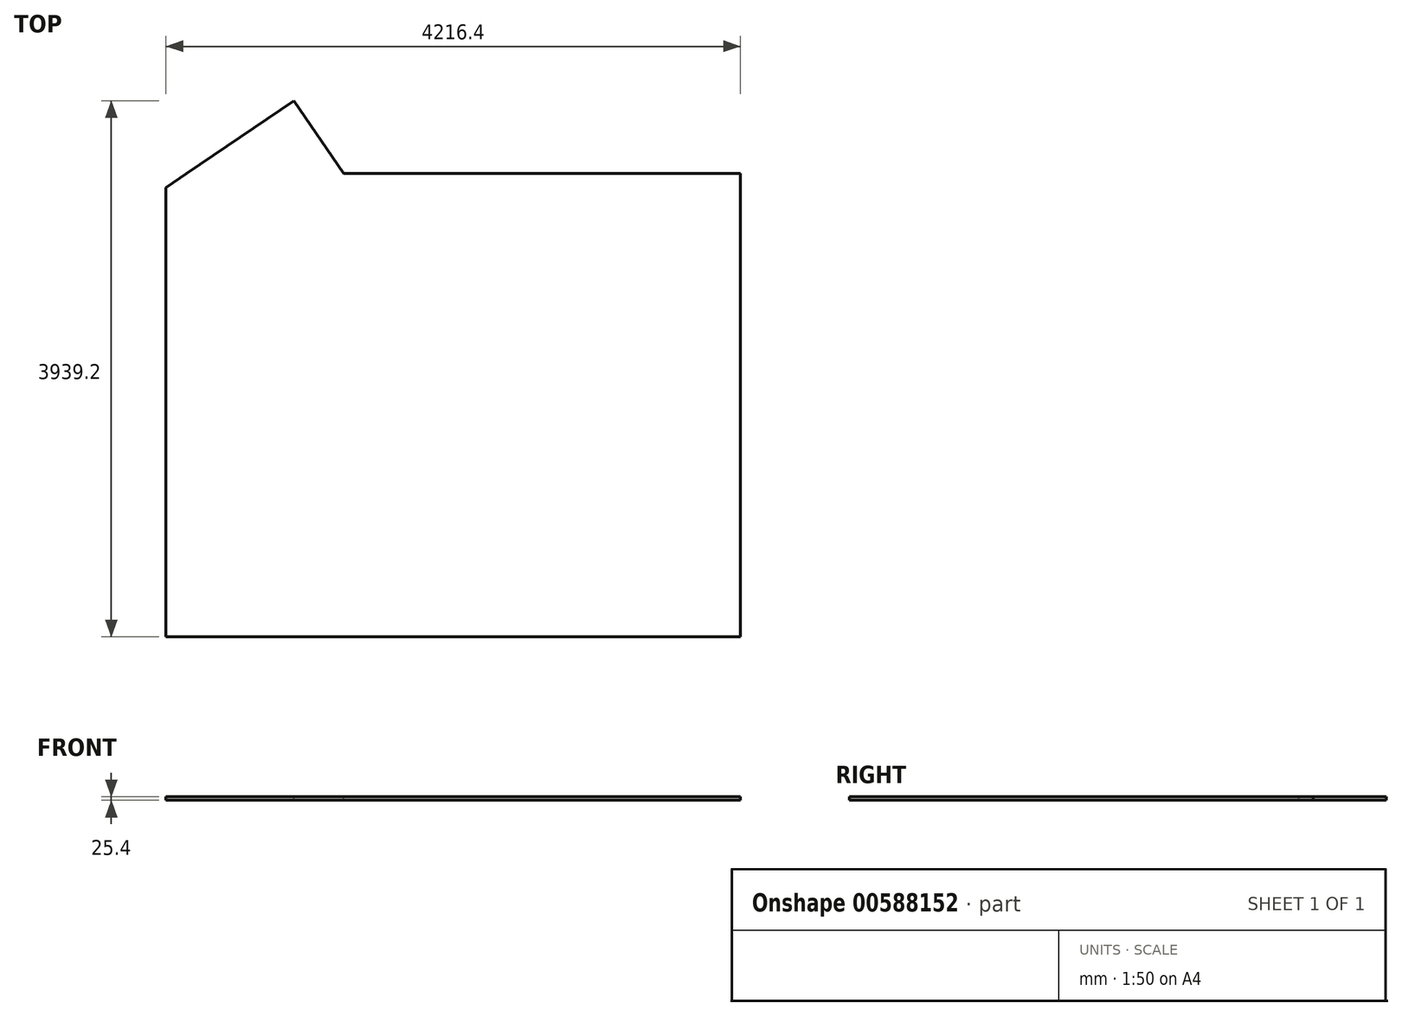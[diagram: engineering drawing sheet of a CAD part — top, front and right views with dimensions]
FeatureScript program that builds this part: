
annotation { "Feature Type Name" : "Feature", "Feature Type Description" : "" }
export const myFeature = defineFeature(function(context is Context, id is Id, definition is map)
    precondition{}
    {
        {
            var Q0;
            Q0=qCreatedBy(makeId("Top.planeOp"),FACE);
            var sketch = newSketch(context, id + "F0", { "sketchPlane" : qUnion([Q0])});
            skLineSegment(sketch, "E0.bottom", {"start": v(2108.2, 1701.8) * mm, "end": v(-2108.2, 1701.8) * mm});
            skLineSegment(sketch, "E0.top", {"start": v(2108.2, -1701.8) * mm, "end": v(-2108.2, -1701.8) * mm});
            skLineSegment(sketch, "E0.left", {"start": v(2108.2, 1701.8) * mm, "end": v(2108.2, -1701.8) * mm});
            skLineSegment(sketch, "E0.right", {"start": v(-2108.2, 1701.8) * mm, "end": v(-2108.2, -1701.8) * mm});
            skPoint(sketch, "E0.middle", {"position": v(0, 0) * mm});
            skSolve(sketch);
        }
        {
            var Q0;
            Q0=makeQuery(id+"F0.imprint","IMPRINT",FACE,{"disambiguationData":[TD([[makeQuery(id+"F0.imprint","IMPRINT",EDGE,{"derivedFrom":sQuery(id+"F0.wireOp",EDGE,"E0.bottom")}),1.0]])]});
            extrude(context, id + "F1", {"entities" : qUnion([Q0]), "depth" : 25.4 * mm, "offsetDistance" : 25.4 * mm});
        }
        {
            var Q0;
            Q0=makeQuery(id+"F1.opExtrude","CAP_FACE",FACE,{"disambiguationData":[OSD([sQuery(id+"F0.wireOp",EDGE,"E0.bottom"),sQuery(id+"F0.wireOp",EDGE,"E0.top"),sQuery(id+"F0.wireOp",EDGE,"E0.left"),sQuery(id+"F0.wireOp",EDGE,"E0.right")])],"isStart":false});
            var sketch = newSketch(context, id + "F2", { "sketchPlane" : qUnion([Q0])});
            skLineSegment(sketch, "E1", {"start": v(-1955.8, 1701.8) * mm, "end": v(-803.94, 1701.8) * mm});
            skLineSegment(sketch, "E2", {"start": v(-803.94, 1701.8) * mm, "end": v(-1168.15, 2237.4) * mm});
            skLineSegment(sketch, "E3", {"start": v(-1168.15, 2237.4) * mm, "end": v(-1955.8, 1701.8) * mm});
            skSolve(sketch);
        }
        {
            var Q0;
            Q0=makeQuery(id+"F2.imprint","IMPRINT",FACE,{"disambiguationData":[TD([[makeQuery(id+"F2.imprint","IMPRINT",EDGE,{"derivedFrom":sQuery(id+"F2.wireOp",EDGE,"E1")}),-1.0]])]});
            extrude(context, id + "F3", {"entities" : qUnion([Q0]), "operationType" : NewBodyOperationType.ADD, "oppositeDirection" : true, "depth" : 25.4 * mm, "offsetDistance" : 25.4 * mm});
        }
        {
            var Q0;
            Q0=makeQuery(id+"F3.boolean.opBoolean","MERGE",FACE,{"derivedFrom":[makeQuery(id+"F1.opExtrude","CAP_FACE",FACE,{"disambiguationData":[OSD([sQuery(id+"F0.wireOp",EDGE,"E0.bottom"),sQuery(id+"F0.wireOp",EDGE,"E0.top"),sQuery(id+"F0.wireOp",EDGE,"E0.left"),sQuery(id+"F0.wireOp",EDGE,"E0.right")])],"isStart":false}),makeQuery(id+"F3.opExtrude","CAP_FACE",FACE,{"disambiguationData":[OSD([sQuery(id+"F2.wireOp",EDGE,"E1"),sQuery(id+"F2.wireOp",EDGE,"E2"),sQuery(id+"F2.wireOp",EDGE,"E3")])],"isStart":true})]});
            var sketch = newSketch(context, id + "F4", { "sketchPlane" : qUnion([Q0])});
            skLineSegment(sketch, "E4", {"start": v(-1955.8, 1701.8) * mm, "end": v(-2108.2, 1701.8) * mm});
            skLineSegment(sketch, "E5", {"start": v(-2108.2, 1701.8) * mm, "end": v(-2108.2, 1598.17) * mm});
            skLineSegment(sketch, "E6", {"start": v(-2108.2, 1598.17) * mm, "end": v(-1955.8, 1701.8) * mm});
            skSolve(sketch);
        }
        {
            var Q0;
            Q0=makeQuery(id+"F4.imprint","IMPRINT",FACE,{"disambiguationData":[TD([[makeQuery(id+"F4.imprint","IMPRINT",EDGE,{"derivedFrom":sQuery(id+"F4.wireOp",EDGE,"E4")}),1.0]])]});
            extrude(context, id + "F5", {"entities" : qUnion([Q0]), "operationType" : NewBodyOperationType.REMOVE, "oppositeDirection" : true, "depth" : 25.4 * mm, "offsetDistance" : 25.4 * mm});
        }
    });
